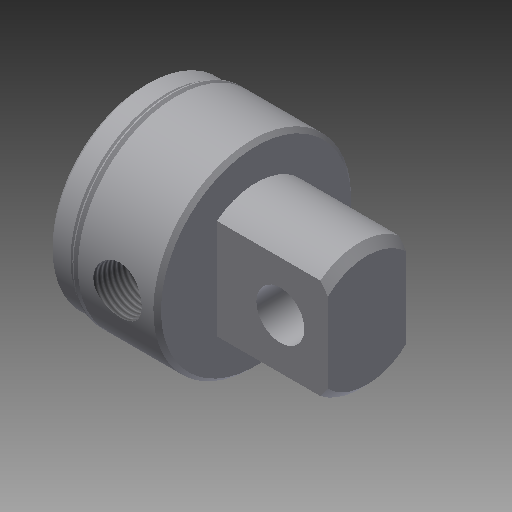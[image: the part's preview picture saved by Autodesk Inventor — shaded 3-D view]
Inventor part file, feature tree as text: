
AUTODESK INVENTOR PART (.ipt)
format: ipt  version: 2019.4 (Build 234330000, 330)  size: 287,744 bytes
history: native  units: in
note: dims shown in document units (in); Inventor stores cm internally (conversion verified against a paired STEP export)
features: other x126, sketch x8, revolve x5, extrude x2, hole x1, thread x1
ambient origin geometry x8: Origin, YZ Plane, XZ Plane, XY Plane, X Axis, Y Axis, Z Axis, Center Point
bodies: Solid1 (feature_tree)
feature tree (143):
  revolve  "Revolution1"  Angle=360.0deg
  revolve  "Revolution2"  Angle=360.0deg
  extrude  "Extrusion1"  TaperAngle=360.0deg  [1 undecoded]
  hole  "Hole1"  [1 undecoded]
  revolve  "Revolution3"  [1 undecoded]
  thread  "Thread1"  [1 undecoded]
  revolve  "Revolution4"  [1 undecoded]
  revolve  "Revolution5"  [1 undecoded]
  extrude  "Extrusion2"  [1 undecoded]
  other  "f_XY"
  other  "f_YZ"
  other  "f_ZX"
  other  "f_X"
  other  "f_Y"
  other  "f_Z"
  other  "f_Center"
  other  "lovra1_XY"
  other  "lovra1_YZ"
  other  "lovra1_ZX"
  other  "lovra1_X"
  other  "lovra1_Y"
  other  "lovra1_Z"
  other  "lovra1_Center"
  other  "lovra2_XY"
  other  "lovra2_YZ"
  other  "lovra2_ZX"
  other  "lovra2_X"
  other  "lovra2_Y"
  other  "lovra2_Z"
  other  "lovra2_Center"
  other  "lovra21_XY"
  other  "lovra21_YZ"
  other  "lovra21_ZX"
  other  "lovra21_X"
  other  "lovra21_Y"
  other  "lovra21_Z"
  other  "lovra21_Center"
  other  "lovra22_XY"
  other  "lovra22_YZ"
  other  "lovra22_ZX"
  other  "lovra22_X"
  other  "lovra22_Y"
  other  "lovra22_Z"
  other  "lovra22_Center"
  other  "lovra3_XY"
  other  "lovra3_YZ"
  other  "lovra3_ZX"
  other  "lovra3_X"
  other  "lovra3_Y"
  other  "lovra3_Z"
  other  "lovra3_Center"
  other  "olen_XY"
  other  "olen_YZ"
  other  "olen_ZX"
  other  "olen_X"
  other  "olen_Y"
  other  "olen_Z"
  other  "olen_Center"
  other  "p1_XY"
  other  "p1_YZ"
  other  "p1_ZX"
  other  "p1_X"
  other  "p1_Y"
  other  "p1_Z"
  other  "p1_Center"
  other  "p2_XY"
  other  "p2_YZ"
  other  "p2_ZX"
  other  "p2_X"
  other  "p2_Y"
  other  "p2_Z"
  other  "p2_Center"
  other  "port_XY"
  other  "port_YZ"
  other  "port_ZX"
  other  "port_X"
  other  "port_Y"
  other  "port_Z"
  other  "port_Center"
  other  "port2_XY"
  other  "port2_YZ"
  other  "port2_ZX"
  other  "port2_X"
  other  "port2_Y"
  other  "port2_Z"
  other  "port2_Center"
  other  "thd1_XY"
  other  "thd1_YZ"
  other  "thd1_ZX"
  other  "thd1_X"
  other  "thd1_Y"
  other  "thd1_Z"
  other  "thd1_Center"
  other  "thd2_XY"
  other  "thd2_YZ"
  other  "thd2_ZX"
  other  "thd2_X"
  other  "thd2_Y"
  other  "thd2_Z"
  other  "thd2_Center"
  other  "to_mounting_bracket_XY"
  other  "to_mounting_bracket_YZ"
  other  "to_mounting_bracket_ZX"
  other  "to_mounting_bracket_X"
  other  "to_mounting_bracket_Y"
  other  "to_mounting_bracket_Z"
  other  "to_mounting_bracket_Center"
  other  "to_nut_XY"
  other  "to_nut_YZ"
  other  "to_nut_ZX"
  other  "to_nut_X"
  other  "to_nut_Y"
  other  "to_nut_Z"
  other  "to_nut_Center"
  other  "to_pin_XY"
  other  "to_pin_YZ"
  other  "to_pin_ZX"
  other  "to_pin_X"
  other  "to_pin_Y"
  other  "to_pin_Z"
  other  "to_pin_Center"
  other  "to_screw_XY"
  other  "to_screw_YZ"
  other  "to_screw_ZX"
  other  "to_screw_X"
  other  "to_screw_Y"
  other  "to_screw_Z"
  other  "to_screw_Center"
  other  "to_tube_XY"
  other  "to_tube_YZ"
  other  "to_tube_ZX"
  other  "to_tube_X"
  other  "to_tube_Y"
  other  "to_tube_Z"
  other  "to_tube_Center"
  sketch  "Sketch_18"  dims[d4=0.532in d5=0.75in d6=0.375in d7=0.25in d8=0.5635in d9=0.8052in d10=120.0deg d11=360.0deg]
  sketch  "Sketch_21"  dims[d15=360.0deg d16=0.9255in d17=0.0in]
  sketch  "Sketch_9"  dims[d2=0.875in d3=0.0in]
  sketch  "Sketch4"  dims[d0=360.0deg d1=360.0deg]
  sketch  "Sketch_68"
  sketch  "Sketch_20"  dims[d12=0.2731in d13=0.0in d14=360.0deg]
  sketch  "Sketch_24"  dims[d18=0.0in d19=0.0in d20=0.0in d21=0.0in d22=0.0in d23=0.0in d24=0.0in d25=0.0in d26=0.0in]
  sketch  "Sketch_43"
note: 7 required parameter values undecoded (feature->parameter linkage not recoverable at this tier; creation-order binding heuristic only, values carry confidence <= 0.55)
